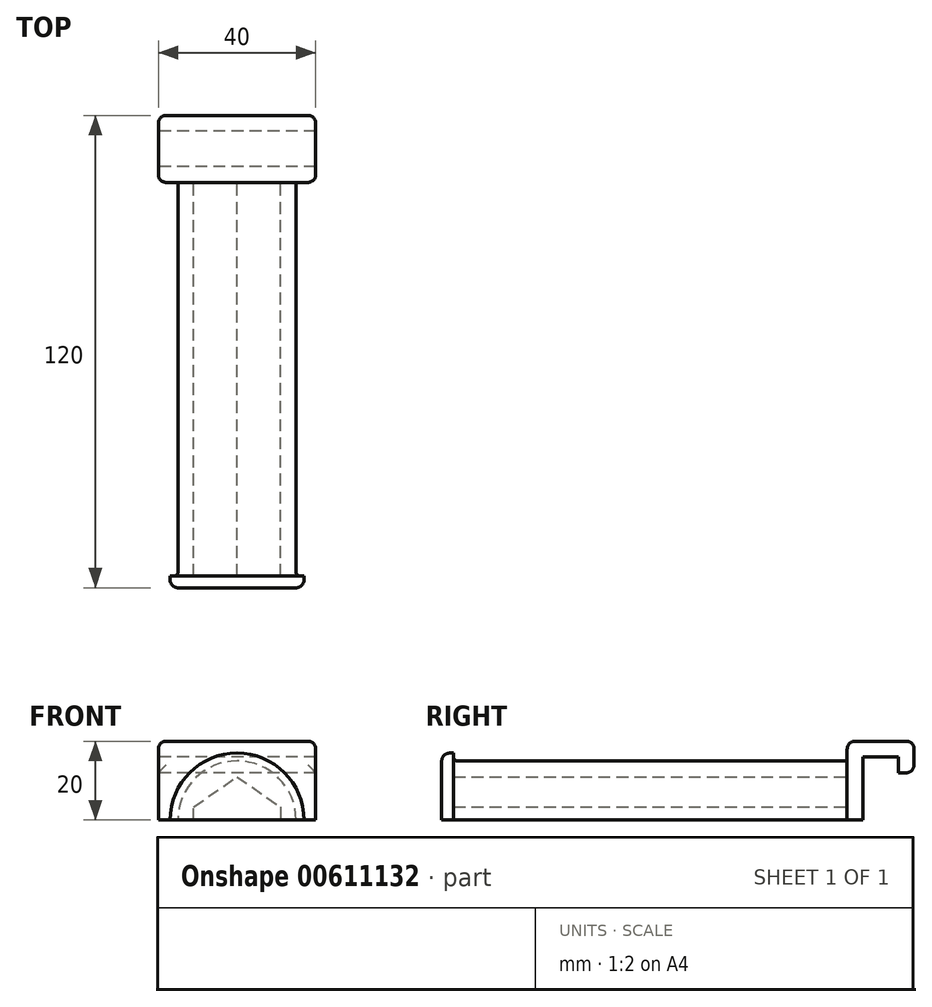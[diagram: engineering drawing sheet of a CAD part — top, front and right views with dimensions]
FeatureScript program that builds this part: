
annotation { "Feature Type Name" : "Feature", "Feature Type Description" : "" }
export const myFeature = defineFeature(function(context is Context, id is Id, definition is map)
    precondition{}
    {
        {
            var Q0;
            Q0=qCreatedBy(makeId("Front.planeOp"),FACE);
            var sketch = newSketch(context, id + "F0", { "sketchPlane" : qUnion([Q0])});
            skArc(sketch, "E0", {"start": v(-15, 0) * mm, "mid": v(0, 15) * mm, "end": v(15, 0) * mm});
            skLineSegment(sketch, "E1", {"start": v(-15, 0) * mm, "end": v(-11, 0) * mm});
            skLineSegment(sketch, "E2", {"start": v(11, 0) * mm, "end": v(15, 0) * mm});
            skLineSegment(sketch, "E3", {"start": v(-11, 0) * mm, "end": v(-11, 3.3) * mm});
            skLineSegment(sketch, "E4", {"start": v(-11, 3.3) * mm, "end": v(0, 11) * mm});
            skLineSegment(sketch, "E5", {"start": v(0, 11) * mm, "end": v(11, 3.3) * mm});
            skLineSegment(sketch, "E6", {"start": v(11, 3.3) * mm, "end": v(11, 0) * mm});
            skSolve(sketch);
        }
        {
            var Q0;
            Q0 = qSketchRegion(id + "F0", true);
            extrude(context, id + "F1", {"entities" : qUnion([Q0]), "depth" : 100 * mm, "offsetDistance" : 25 * mm});
        }
        {
            var Q0;
            Q0=qCreatedBy(makeId("Right.planeOp"),FACE);
            var sketch = newSketch(context, id + "F2", { "sketchPlane" : qUnion([Q0])});
            skLineSegment(sketch, "E7", {"start": v(0, 0) * mm, "end": v(0, 20) * mm});
            skLineSegment(sketch, "E8", {"start": v(0, 20) * mm, "end": v(17, 20) * mm});
            skLineSegment(sketch, "E9", {"start": v(17, 20) * mm, "end": v(17, 12) * mm});
            skLineSegment(sketch, "E10", {"start": v(17, 12) * mm, "end": v(13, 12) * mm});
            skLineSegment(sketch, "E11", {"start": v(13, 12) * mm, "end": v(13, 16) * mm});
            skLineSegment(sketch, "E12", {"start": v(13, 16) * mm, "end": v(4, 16) * mm});
            skLineSegment(sketch, "E13", {"start": v(4, 16) * mm, "end": v(4, 0) * mm});
            skLineSegment(sketch, "E14", {"start": v(4, 0) * mm, "end": v(0, 0) * mm});
            skSolve(sketch);
        }
        {
            var Q0;
            Q0 = qSketchRegion(id + "F2", true);
            extrude(context, id + "F3", {"entities" : qUnion([Q0]), "operationType" : NewBodyOperationType.ADD, "endBound" : BoundingType.SYMMETRIC, "depth" : 40 * mm, "offsetDistance" : 25 * mm});
        }
        {
            var Q0;
            Q0=makeQuery(id+"F1.opExtrude","CAP_FACE",FACE,{"disambiguationData":[OSD([sQuery(id+"F0.wireOp",EDGE,"E0"),sQuery(id+"F0.wireOp",EDGE,"E1"),sQuery(id+"F0.wireOp",EDGE,"E2"),sQuery(id+"F0.wireOp",EDGE,"E3"),sQuery(id+"F0.wireOp",EDGE,"E4"),sQuery(id+"F0.wireOp",EDGE,"E5"),sQuery(id+"F0.wireOp",EDGE,"E6")])],"isStart":false});
            var sketch = newSketch(context, id + "F4", { "sketchPlane" : qUnion([Q0])});
            skArc(sketch, "E15", {"start": v(-17, 0) * mm, "mid": v(0, 17) * mm, "end": v(17, 0) * mm});
            skLineSegment(sketch, "E16", {"start": v(-17, 0) * mm, "end": v(17, 0) * mm});
            skSolve(sketch);
        }
        {
            var Q0;
            Q0 = qSketchRegion(id + "F4", true);
            extrude(context, id + "F5", {"entities" : qUnion([Q0]), "operationType" : NewBodyOperationType.ADD, "depth" : 3 * mm, "offsetDistance" : 25 * mm});
        }
        {
            var Q0;
            Q0=makeQuery(id+"F3.opExtrude","SWEPT_EDGE",EDGE,{"disambiguationData":[OSD([sQuery(id+"F2.wireOp",EDGE,"E8"),sQuery(id+"F2.wireOp",EDGE,"E9")])]});
            var Q1;
            Q1=makeQuery(id+"F3.opExtrude","SWEPT_EDGE",EDGE,{"disambiguationData":[OSD([sQuery(id+"F2.wireOp",EDGE,"E7"),sQuery(id+"F2.wireOp",EDGE,"E8")])]});
            var Q2;
            Q2=makeQuery(id+"F3.opExtrude","CAP_EDGE",EDGE,{"disambiguationData":[OSD([sQuery(id+"F2.wireOp",EDGE,"E8")])],"isStart":false});
            var Q3;
            Q3=makeQuery(id+"F3.opExtrude","CAP_EDGE",EDGE,{"disambiguationData":[OSD([sQuery(id+"F2.wireOp",EDGE,"E8")])],"isStart":true});
            var Q4;
            Q4=makeQuery(id+"F3.opExtrude","SWEPT_EDGE",EDGE,{"disambiguationData":[OSD([sQuery(id+"F2.wireOp",EDGE,"E9"),sQuery(id+"F2.wireOp",EDGE,"E10")])]});
            var Q5;
            Q5=makeQuery(id+"F3.opExtrude","CAP_EDGE",EDGE,{"disambiguationData":[OSD([sQuery(id+"F2.wireOp",EDGE,"E7")])],"isStart":false});
            var Q6;
            Q6=makeQuery(id+"F3.opExtrude","CAP_EDGE",EDGE,{"disambiguationData":[OSD([sQuery(id+"F2.wireOp",EDGE,"E7")])],"isStart":true});
            var Q7;
            Q7=makeQuery(id+"F3.opExtrude","CAP_EDGE",EDGE,{"disambiguationData":[OSD([sQuery(id+"F2.wireOp",EDGE,"E9")])],"isStart":true});
            var Q8;
            Q8=makeQuery(id+"F3.opExtrude","CAP_EDGE",EDGE,{"disambiguationData":[OSD([sQuery(id+"F2.wireOp",EDGE,"E9")])],"isStart":false});
            var Q9;
            Q9=makeQuery(id+"F5.opExtrude","CAP_EDGE",EDGE,{"disambiguationData":[OSD([sQuery(id+"F4.wireOp",EDGE,"E15")])],"isStart":false});
            fillet(context, id + "F6", {"entities" : qUnion([Q0, Q1, Q2, Q3, Q4, Q5, Q6, Q7, Q8, Q9]), "radius" : 2 * mm, "tangentPropagation" : true, "allowEdgeOverflow" : false});
        }
        {
            var Q0;
            Q0=makeQuery(id+"F1.opExtrude","CAP_EDGE",EDGE,{"disambiguationData":[OSD([sQuery(id+"F0.wireOp",EDGE,"E0")])],"isStart":true});
            var Q1;
            Q1=makeQuery(id+"F1.opExtrude","CAP_EDGE",EDGE,{"disambiguationData":[OSD([sQuery(id+"F0.wireOp",EDGE,"E0")])],"isStart":false});
            fillet(context, id + "F7", {"entities" : qUnion([Q0, Q1]), "radius" : 1 * mm, "tangentPropagation" : true, "allowEdgeOverflow" : false});
        }
    });
